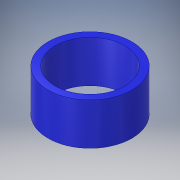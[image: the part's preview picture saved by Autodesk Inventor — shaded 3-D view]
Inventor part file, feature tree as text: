
AUTODESK INVENTOR PART (.ipt)
format: ipt  version: 2018 (Build 220112000, 112)  size: 125,952 bytes
history: native  units: in
note: dims shown in document units (in); Inventor stores cm internally (conversion verified against a paired STEP export)
features: revolve x1, sketch x1
ambient origin geometry x8: Origin, YZ Plane, XZ Plane, XY Plane, X Axis, Y Axis, Z Axis, Center Point
bodies: Solid1 (feature_tree)
feature tree (2):
  revolve  "Revolution1"  [1 undecoded]
  sketch  "Sketch1"  dims[d0=1.5625in d1=5.0in d3=14.0in d4=90.0deg d5=1.5in d6=1.5in d7=2.5in d9=0.75in d10=0.25in d11=0.75in d12=0.25in]
note: 1 required parameter value undecoded (feature->parameter linkage not recoverable at this tier; creation-order binding heuristic only, values carry confidence <= 0.55)
